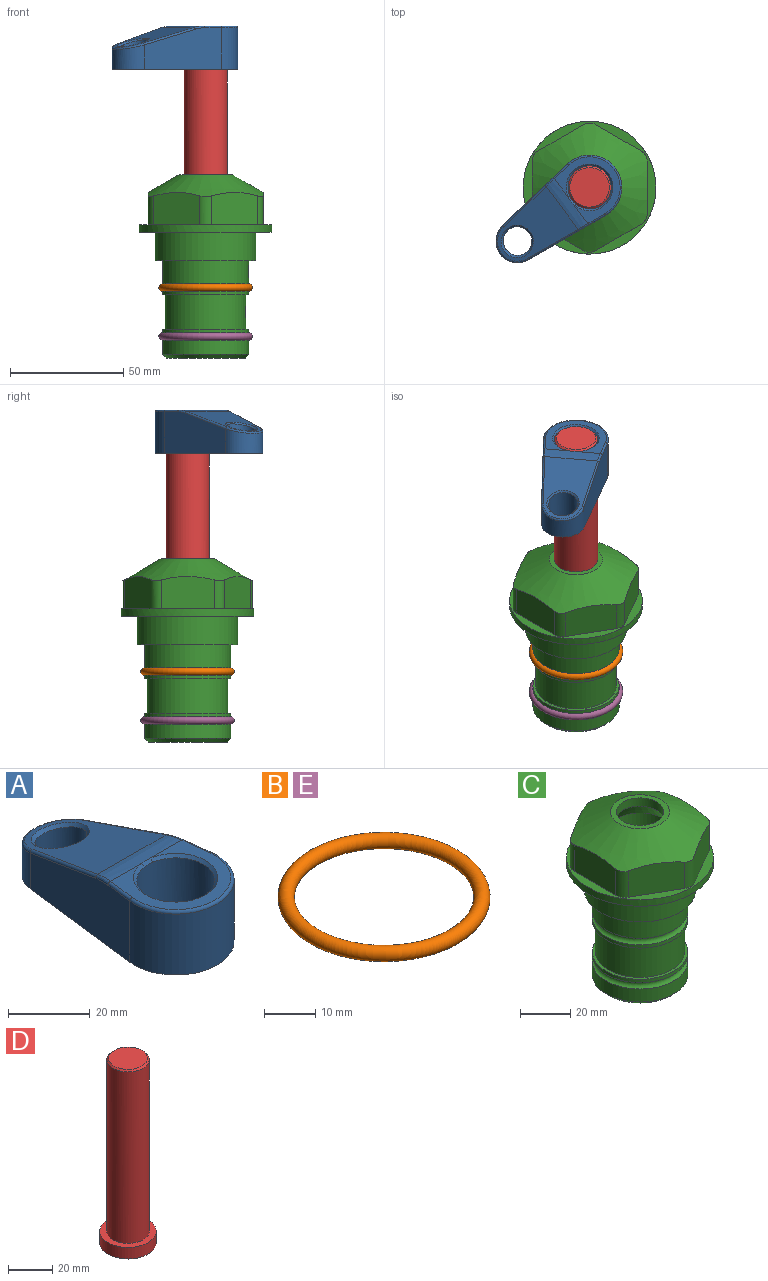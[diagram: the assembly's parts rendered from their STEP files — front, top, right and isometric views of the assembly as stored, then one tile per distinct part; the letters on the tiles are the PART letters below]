
ASSEMBLY  parts=5 mates=4
PART A: 31 faces, bbox 31.7x65.5x19.8 mm
  f0: plane 39.12x18.26mm, normal (0.99,0.12,0), area 612.2mm2, adj f1,f4,f7,f11,f13,f15
  f1: cylinder r=9.53mm len=18.91mm, axis (0,0,-1), area 296.1mm2, adj f0,f2,f7,f17
  f2: plane 39.12x18.26mm, normal (-0.99,0.12,0), area 612.2mm2, adj f1,f4,f7,f12,f14,f16
  f3: cylinder r=6.35mm len=12.7mm, axis (0,0,-1), area 362.4mm2, adj f7,f18
  f4: cylinder r=14.29mm len=28.58mm, axis (0,0,-1), area 882.2mm2, adj f0,f2,f7,f10
  f5: cylinder r=9.53mm len=19.05mm, axis (0,0,-1), area 1092.6mm2, adj f7,f19,f20
  f6: plane 26.99x23.69mm, normal (0,0,1), area 216.2mm2, adj f9,f10,f11,f12,f19
  f7: plane 63.5x28.58mm, normal (0,0,-1), area 661.8mm2, adj f0,f1,f2,f3,f4,f5,f22,f23
  f8: plane 33.52x23.6mm, normal (0,0.26,0.97), area 486mm2, adj f9,f15,f16,f17,f18
  f9: cylinder r=19.05mm len=24.72mm, axis (1,0,0), area 120.4mm2, adj f6,f8,f13,f14,f20
  f10: torus R=13.49mm, axis (0,0,1), area 59mm2, adj f4,f6,f11,f12
  f11: cylinder r=0.79mm len=8.67mm, axis (0.12,-0.99,0), area 10.8mm2, adj f0,f6,f10,f13
  f12: cylinder r=0.79mm len=8.67mm, axis (0.12,0.99,0), area 10.8mm2, adj f2,f6,f10,f14
  f13: bspline ~4.95x1.42mm, area 6.1mm2, adj f0,f9,f11,f15
  f14: bspline ~4.95x1.42mm, area 6.1mm2, adj f2,f9,f12,f16
  f15: cylinder r=0.79mm len=25.95mm, axis (0.12,-0.96,0.26), area 32.9mm2, adj f0,f8,f13,f17
  f16: cylinder r=0.79mm len=25.95mm, axis (0.12,0.96,-0.26), area 32.9mm2, adj f2,f8,f14,f17
  f17: bspline ~18.91x8.38mm, area 30mm2, adj f1,f8,f15,f16
  f18: bspline ~14.29x14.29mm, area 48.3mm2, adj f3,f8
  f19: cone r=9.53mm half-angle=45deg, axis (0,0,1), area 66.5mm2, adj f5,f6,f20
  f20: bspline ~3.22x0.96mm, area 3.5mm2, adj f5,f9,f19
  f21: plane 2.75x2.72mm, normal (0,0,-1), area 2.9mm2, adj f23,f25,f28
  f22: plane 23.05x15.88mm, normal (-0.99,-0.12,0), area 323.6mm2, adj f7,f25,f26,f27,f28,f29
  f23: plane 23.05x15.88mm, normal (0.99,-0.12,0), area 323.6mm2, adj f7,f21,f25,f27,f28,f30
  f24: cylinder r=9.53mm len=10.69mm, axis (0,0,-1), area 114.7mm2, adj f7,f27,f29,f30
  f25: cylinder r=12.7mm len=20.59mm, axis (0,0,-1), area 381.1mm2, adj f7,f21,f22,f23,f26,f28
  f26: plane 2.75x2.72mm, normal (0,0,-1), area 2.9mm2, adj f22,f25,f28
  f27: plane 19.72x18.37mm, normal (0,-0.26,-0.97), area 291.8mm2, adj f22,f23,f24,f28,f29,f30
  f28: cylinder r=15.88mm len=19.92mm, axis (1,0,0), area 54.8mm2, adj f21,f22,f23,f25,f26,f27
  f29: cylinder r=1.59mm len=11mm, axis (0,0,-1), area 34.7mm2, adj f7,f22,f24,f27
  f30: cylinder r=1.59mm len=11mm, axis (0,0,-1), area 34.7mm2, adj f7,f23,f24,f27
PART B: 1 faces, bbox 44.7x44.7x3.2 mm
  f0: torus R=19.05mm, axis (0,0,1), area 1193.9mm2
PART C: 36 faces, bbox 58.7x58.7x81 mm
  f0: cylinder r=17.78mm len=35.56mm, axis (0,0,1), area 1670.8mm2, adj f23,f24,f31
  f1: cylinder r=19.05mm len=38.1mm, axis (0,0,1), area 1191.9mm2, adj f26,f27,f30
  f2: plane 58.66x58.66mm, normal (0,0,-1), area 1150.6mm2, adj f3,f28
  f3: cylinder r=29.33mm len=58.66mm, axis (0,0,-1), area 585.1mm2, adj f2,f4
  f4: plane 58.66x58.66mm, normal (0,0,1), area 475.9mm2, adj f3,f5,f6,f7,f8,f9,f10,f11
  f5: plane 20.32x14.34mm, normal (-0.5,0.87,0), area 324.4mm2, adj f4,f15,f16,f17
  f6: plane 20.32x14.34mm, normal (0.5,0.87,0), area 324.4mm2, adj f4,f14,f15,f17
  f7: plane 23.48x14.34mm, normal (1,0,0), area 324.4mm2, adj f4,f13,f14,f17
  f8: plane 20.32x14.34mm, normal (0.5,-0.87,0), area 324.4mm2, adj f4,f12,f13,f17
  f9: plane 20.32x14.34mm, normal (-0.5,-0.87,0), area 324.4mm2, adj f4,f11,f12,f17
  f10: plane 23.48x14.34mm, normal (-1,0,0), area 324.4mm2, adj f4,f11,f16,f17
  f11: cylinder r=5.08mm len=12.85mm, axis (0,0,-1), area 67.2mm2, adj f4,f9,f10,f17
  f12: cylinder r=5.08mm len=12.85mm, axis (0,0,-1), area 67.2mm2, adj f4,f8,f9,f17
  f13: cylinder r=5.08mm len=12.85mm, axis (0,0,-1), area 67.2mm2, adj f4,f7,f8,f17
  f14: cylinder r=5.08mm len=12.85mm, axis (0,0,-1), area 67.2mm2, adj f4,f6,f7,f17
  f15: cylinder r=5.08mm len=12.85mm, axis (0,0,-1), area 67.2mm2, adj f4,f5,f6,f17
  f16: cylinder r=5.08mm len=12.85mm, axis (0,0,-1), area 67.2mm2, adj f4,f5,f10,f17
  f17: cone r=11.73mm half-angle=60deg, axis (0,0,-1), area 2071.8mm2, adj f5,f6,f7,f8,f9,f10,f11,f12
  f18: plane 23.46x23.46mm, normal (0,0,1), area 147.4mm2, adj f17,f35
  f19: plane 34.93x34.93mm, normal (0,0,-1), area 958mm2, adj f29
  f20: cylinder r=19.05mm len=38.1mm, axis (0,0,1), area 760.1mm2, adj f21,f29
  f21: torus R=19.05mm, axis (0,0,1), area 565.3mm2, adj f20,f22
  f22: cylinder r=19.05mm len=38.1mm, axis (0,0,1), area 190mm2, adj f21,f23
  f23: plane 38.1x38.1mm, normal (0,0,1), area 146.9mm2, adj f0,f22
  f24: plane 38.1x38.1mm, normal (0,0,-1), area 146.9mm2, adj f0,f25
  f25: cylinder r=19.05mm len=38.1mm, axis (0,0,1), area 190mm2, adj f24,f26
  f26: torus R=19.05mm, axis (0,0,1), area 565.3mm2, adj f1,f25
  f27: plane 44.45x44.45mm, normal (0,0,-1), area 411.7mm2, adj f1,f28
  f28: cylinder r=22.23mm len=44.45mm, axis (0,0,1), area 1773.5mm2, adj f2,f27
  f29: cone r=19.05mm half-angle=45deg, axis (0,0,1), area 257.5mm2, adj f19,f20
  f30: cylinder r=3.17mm len=6.75mm, axis (-1,0,0), area 128mm2, adj f1,f33
  f31: cylinder r=3.17mm len=6.35mm, axis (-1,0,0), area 102.5mm2, adj f0,f33
  f32: plane 25.4x25.4mm, normal (0,0,1), area 506.7mm2, adj f33
  f33: cylinder r=12.7mm len=66.42mm, axis (0,0,-1), area 5236.2mm2, adj f30,f31,f32,f34
  f34: cone r=9.53mm half-angle=30deg, axis (0,0,-1), area 443.4mm2, adj f33,f35
  f35: cylinder r=9.53mm len=19.05mm, axis (0,0,-1), area 240.9mm2, adj f18,f34
PART D: 6 faces, bbox 25.4x25.4x101.6 mm
  f0: plane 17.46x17.46mm, normal (0,0,1), area 239.5mm2, adj f5
  f1: plane 25.4x25.4mm, normal (0,0,-1), area 506.7mm2, adj f2
  f2: cylinder r=12.7mm len=25.4mm, axis (0,0,1), area 506.7mm2, adj f1,f3
  f3: plane 25.4x25.4mm, normal (0,0,1), area 221.7mm2, adj f2,f4
  f4: cylinder r=9.53mm len=94.46mm, axis (0,0,1), area 5653mm2, adj f3,f5
  f5: cone r=8.73mm half-angle=45deg, axis (0,0,-1), area 64.4mm2, adj f0,f4
PART E: same geometry as B
PLACE A rot(axis=(0,0,1),126.7deg) t=(0,0,27.55)mm
PLACE B at identity
PLACE C at identity fixed
PLACE D rot(axis=(0,0,1),126.7deg) t=(0,0,27.55)mm
PLACE E t=(0,0,-21.59)mm
MATE fastened E.f0 <-> C.f0  axis (0,0,1) through (0,0,-46.1)mm
MATE cylindrical D.f2 <-> C.f0  axis (0,0,-1) through (0,0,-10.55)mm
MATE fastened C.f0 <-> B.f0  axis (0,0,1) through (0,0,-24.51)mm
MATE fastened A.f4 <-> D.f2  axis (0,0,1) through (0,0,91.05)mm
